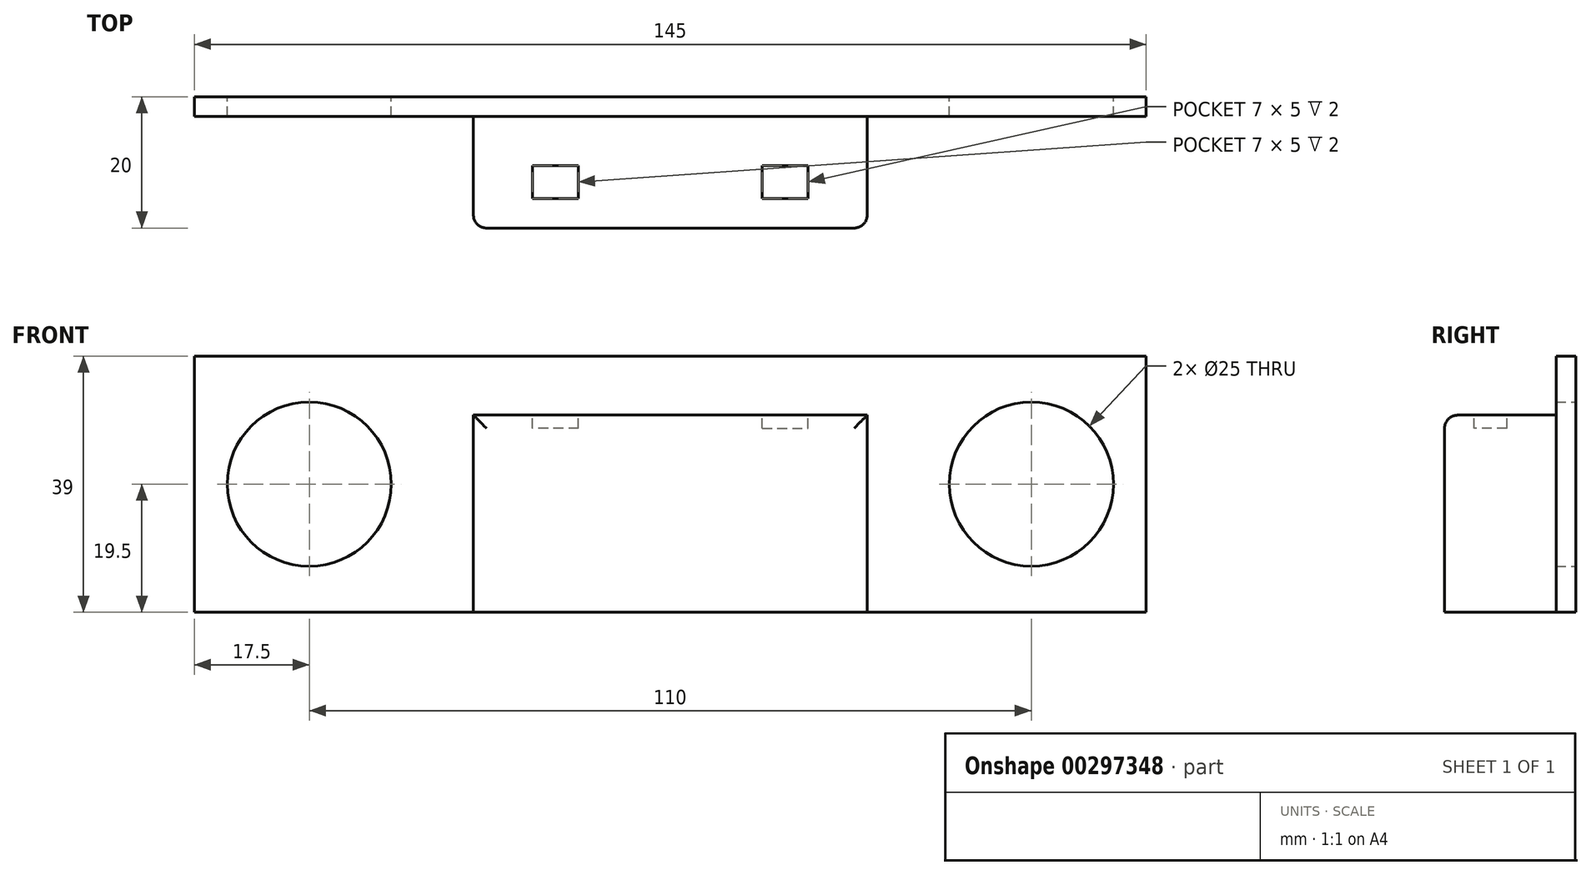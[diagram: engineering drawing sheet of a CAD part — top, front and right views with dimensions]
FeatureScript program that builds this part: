
annotation { "Feature Type Name" : "Feature", "Feature Type Description" : "" }
export const myFeature = defineFeature(function(context is Context, id is Id, definition is map)
    precondition{}
    {
        {
            var Q0;
            Q0=qCreatedBy(makeId("Front.planeOp"),FACE);
            var sketch = newSketch(context, id + "F0", { "sketchPlane" : qUnion([Q0])});
            skLineSegment(sketch, "E0.bottom", {"start": v(72.5, 19.5) * mm, "end": v(-72.5, 19.5) * mm});
            skLineSegment(sketch, "E0.top", {"start": v(72.5, -19.5) * mm, "end": v(-72.5, -19.5) * mm});
            skLineSegment(sketch, "E0.left", {"start": v(72.5, 19.5) * mm, "end": v(72.5, -19.5) * mm});
            skLineSegment(sketch, "E0.right", {"start": v(-72.5, 19.5) * mm, "end": v(-72.5, -19.5) * mm});
            skPoint(sketch, "E0.middle", {"position": v(0, 0) * mm});
            skCircle(sketch, "E1", {"center": v(-55, 0) * mm, "radius": 12.5 * mm});
            skCircle(sketch, "E2", {"center": v(55, 0) * mm, "radius": 12.5 * mm});
            skSolve(sketch);
        }
        {
            var Q0;
            Q0=qSketchRegion(id+"F0",true);
            extrude(context, id + "F1", {"entities" : qUnion([Q0]), "depth" : 3 * mm});
        }
        {
            var Q0;
            Q0=makeQuery(id+"F1.opExtrude","CAP_FACE",FACE,{"disambiguationData":[OSD([sQuery(id+"F0.wireOp",EDGE,"E0.bottom"),sQuery(id+"F0.wireOp",EDGE,"E0.top"),sQuery(id+"F0.wireOp",EDGE,"E0.left"),sQuery(id+"F0.wireOp",EDGE,"E0.right"),sQuery(id+"F0.wireOp",EDGE,"E1"),sQuery(id+"F0.wireOp",EDGE,"E2")])],"isStart":false});
            var sketch = newSketch(context, id + "F2", { "sketchPlane" : qUnion([Q0])});
            skLineSegment(sketch, "E3.bottom", {"start": v(-30, 10.5) * mm, "end": v(30, 10.5) * mm});
            skLineSegment(sketch, "E3.top", {"start": v(-30, -19.5) * mm, "end": v(30, -19.5) * mm});
            skLineSegment(sketch, "E3.left", {"start": v(-30, 10.5) * mm, "end": v(-30, -19.5) * mm});
            skLineSegment(sketch, "E3.right", {"start": v(30, 10.5) * mm, "end": v(30, -19.5) * mm});
            skSolve(sketch);
        }
        {
            var Q0;
            Q0 = qSketchRegion(id + "F2", true);
            extrude(context, id + "F3", {"entities" : qUnion([Q0]), "operationType" : NewBodyOperationType.ADD, "depth" : 17 * mm});
        }
        {
            var Q0;
            Q0=makeQuery(id+"F3.opExtrude","SWEPT_FACE",FACE,{"disambiguationData":[OSD([sQuery(id+"F2.wireOp",EDGE,"E3.bottom")])]});
            var sketch = newSketch(context, id + "F4", { "sketchPlane" : qUnion([Q0])});
            skLineSegment(sketch, "E4.bottom", {"start": v(17.5, -13) * mm, "end": v(-17.5, -13) * mm, "construction": true});
            skLineSegment(sketch, "E4.top", {"start": v(17.5, -13) * mm, "end": v(-17.5, -13) * mm, "construction": true});
            skLineSegment(sketch, "E4.left", {"start": v(17.5, -13) * mm, "end": v(17.5, -13) * mm});
            skLineSegment(sketch, "E4.right", {"start": v(-17.5, -13) * mm, "end": v(-17.5, -13) * mm});
            skPoint(sketch, "E4.middle", {"position": v(0, -13) * mm});
            skLineSegment(sketch, "E5.bottom", {"start": v(-14, -10.5) * mm, "end": v(-21, -10.5) * mm});
            skLineSegment(sketch, "E5.top", {"start": v(-14, -15.5) * mm, "end": v(-21, -15.5) * mm});
            skLineSegment(sketch, "E5.left", {"start": v(-14, -10.5) * mm, "end": v(-14, -15.5) * mm});
            skLineSegment(sketch, "E5.right", {"start": v(-21, -10.5) * mm, "end": v(-21, -15.5) * mm});
            skPoint(sketch, "E5.middle", {"position": v(-17.5, -13) * mm});
            skLineSegment(sketch, "E6.bottom", {"start": v(14, -10.5) * mm, "end": v(21, -10.5) * mm});
            skLineSegment(sketch, "E6.top", {"start": v(14, -15.5) * mm, "end": v(21, -15.5) * mm});
            skLineSegment(sketch, "E6.left", {"start": v(14, -10.5) * mm, "end": v(14, -15.5) * mm});
            skLineSegment(sketch, "E6.right", {"start": v(21, -10.5) * mm, "end": v(21, -15.5) * mm});
            skPoint(sketch, "E6.middle", {"position": v(17.5, -13) * mm});
            skSolve(sketch);
        }
        {
            var Q0;
            Q0 = qSketchRegion(id + "F4", true);
            extrude(context, id + "F5", {"entities" : qUnion([Q0]), "operationType" : NewBodyOperationType.REMOVE, "oppositeDirection" : true, "depth" : 2 * mm});
        }
        {
            var Q0;
            Q0=makeQuery(id+"F3.opExtrude","CAP_EDGE",EDGE,{"disambiguationData":[OSD([sQuery(id+"F2.wireOp",EDGE,"E3.bottom")])],"isStart":true});
            var Q1;
            Q1=makeQuery(id+"F3.opExtrude","CAP_EDGE",EDGE,{"disambiguationData":[OSD([sQuery(id+"F2.wireOp",EDGE,"E3.right")])],"isStart":true});
            var Q2;
            Q2=makeQuery(id+"F3.opExtrude","CAP_EDGE",EDGE,{"disambiguationData":[OSD([sQuery(id+"F2.wireOp",EDGE,"E3.left")])],"isStart":true});
            var Q3;
            Q3=makeQuery(id+"F3.opExtrude","CAP_EDGE",EDGE,{"disambiguationData":[OSD([sQuery(id+"F2.wireOp",EDGE,"E3.left")])],"isStart":false});
            var Q4;
            Q4=makeQuery(id+"F3.opExtrude","CAP_EDGE",EDGE,{"disambiguationData":[OSD([sQuery(id+"F2.wireOp",EDGE,"E3.bottom")])],"isStart":false});
            var Q5;
            Q5=makeQuery(id+"F3.opExtrude","CAP_EDGE",EDGE,{"disambiguationData":[OSD([sQuery(id+"F2.wireOp",EDGE,"E3.right")])],"isStart":false});
            fillet(context, id + "F6", {"entities" : qUnion([Q0, Q1, Q2, Q3, Q4, Q5]), "radius" : 2 * mm, "tangentPropagation" : true, "allowEdgeOverflow" : false});
        }
    });
